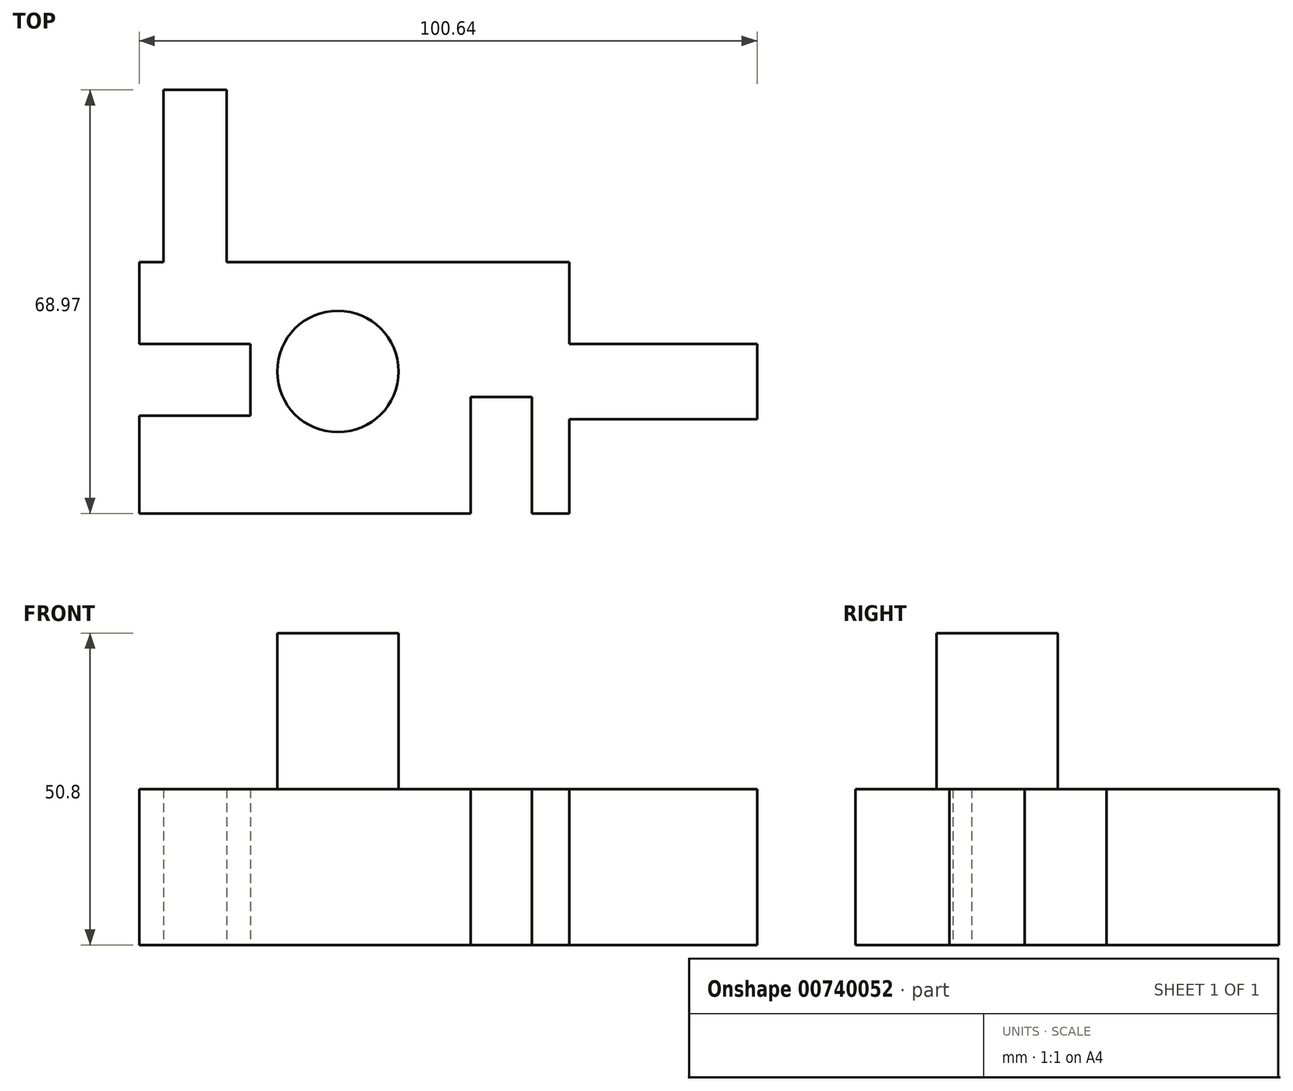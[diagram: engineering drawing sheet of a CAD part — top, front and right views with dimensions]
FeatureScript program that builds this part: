
annotation { "Feature Type Name" : "Feature", "Feature Type Description" : "" }
export const myFeature = defineFeature(function(context is Context, id is Id, definition is map)
    precondition{}
    {
        {
            var Q0;
            Q0=qCreatedBy(makeId("Top.planeOp"),FACE);
            var sketch = newSketch(context, id + "F0", { "sketchPlane" : qUnion([Q0])});
            skLineSegment(sketch, "E0.bottom", {"start": v(0, 0) * mm, "end": v(70.08, 0) * mm});
            skLineSegment(sketch, "E0.top", {"start": v(0, 40.9) * mm, "end": v(70.08, 40.9) * mm});
            skLineSegment(sketch, "E0.left", {"start": v(0, 0) * mm, "end": v(0, 40.9) * mm});
            skLineSegment(sketch, "E0.right", {"start": v(70.08, 0) * mm, "end": v(70.08, 40.9) * mm});
            skLineSegment(sketch, "E1.bottom", {"start": v(70.08, 15.35) * mm, "end": v(100.64, 15.35) * mm});
            skLineSegment(sketch, "E1.top", {"start": v(70.08, 27.57) * mm, "end": v(100.64, 27.57) * mm});
            skLineSegment(sketch, "E1.left", {"start": v(70.08, 15.35) * mm, "end": v(70.08, 27.57) * mm});
            skLineSegment(sketch, "E1.right", {"start": v(100.64, 15.35) * mm, "end": v(100.64, 27.57) * mm});
            skLineSegment(sketch, "E2.bottom", {"start": v(3.96, 40.9) * mm, "end": v(14.24, 40.9) * mm});
            skLineSegment(sketch, "E2.top", {"start": v(3.96, 68.97) * mm, "end": v(14.24, 68.97) * mm});
            skLineSegment(sketch, "E2.left", {"start": v(3.96, 40.9) * mm, "end": v(3.96, 68.97) * mm});
            skLineSegment(sketch, "E2.right", {"start": v(14.24, 40.9) * mm, "end": v(14.24, 68.97) * mm});
            skLineSegment(sketch, "E3.bottom", {"start": v(0, 27.57) * mm, "end": v(18.13, 27.57) * mm});
            skLineSegment(sketch, "E3.top", {"start": v(0, 15.9) * mm, "end": v(18.13, 15.9) * mm});
            skLineSegment(sketch, "E3.left", {"start": v(0, 27.57) * mm, "end": v(0, 15.9) * mm});
            skLineSegment(sketch, "E3.right", {"start": v(18.13, 27.57) * mm, "end": v(18.13, 15.9) * mm});
            skLineSegment(sketch, "E4.bottom", {"start": v(53.97, 0) * mm, "end": v(63.97, 0) * mm});
            skLineSegment(sketch, "E4.top", {"start": v(53.97, 18.96) * mm, "end": v(63.97, 18.96) * mm});
            skLineSegment(sketch, "E4.left", {"start": v(53.97, 0) * mm, "end": v(53.97, 18.96) * mm});
            skLineSegment(sketch, "E4.right", {"start": v(63.97, 0) * mm, "end": v(63.97, 18.96) * mm});
            skSolve(sketch);
        }
        {
            var Q0;
            {var subQ2=sQuery(id+"F0.wireOp",EDGE,"E1.bottom");Q0=makeQuery(id+"F0.imprint","IMPRINT",FACE,{"disambiguationData":[TD([[makeQuery(id+"F0.imprint","IMPRINT",EDGE,{"derivedFrom":subQ2}),1.0]])]});}
            var Q1;
            Q1=makeQuery(id+"F0.imprint","IMPRINT",FACE,{"disambiguationData":[TD([[makeQuery(id+"F0.imprint","IMPRINT",EDGE,{"derivedFrom":sQuery(id+"F0.wireOp",EDGE,"E2.top")}),-1.0]])]});
            var Q2;
            {var subQ7=sQuery(id+"F0.wireOp",EDGE,"E3.bottom");Q2=makeQuery(id+"F0.imprint","IMPRINT",FACE,{"disambiguationData":[TD([[makeQuery(id+"F0.imprint","IMPRINT",EDGE,{"derivedFrom":subQ7}),1.0]])]});}
            extrude(context, id + "F1", {"entities" : qUnion([Q0, Q1, Q2]), "depth" : 25.4 * mm, "offsetDistance" : 25.4 * mm});
        }
        {
            var Q0;
            Q0=makeQuery(id+"F1.opExtrude","CAP_FACE",FACE,{"disambiguationData":[OSD([sQuery(id+"F0.wireOp",EDGE,"E0.bottom"),sQuery(id+"F0.wireOp",EDGE,"E0.top"),sQuery(id+"F0.wireOp",EDGE,"E0.left"),sQuery(id+"F0.wireOp",EDGE,"E0.right"),sQuery(id+"F0.wireOp",EDGE,"E1.bottom"),sQuery(id+"F0.wireOp",EDGE,"E1.top"),sQuery(id+"F0.wireOp",EDGE,"E1.right"),sQuery(id+"F0.wireOp",EDGE,"E2.top"),sQuery(id+"F0.wireOp",EDGE,"E2.left"),sQuery(id+"F0.wireOp",EDGE,"E2.right"),sQuery(id+"F0.wireOp",EDGE,"E3.bottom"),sQuery(id+"F0.wireOp",EDGE,"E3.top"),sQuery(id+"F0.wireOp",EDGE,"E3.right"),sQuery(id+"F0.wireOp",EDGE,"E4.top"),sQuery(id+"F0.wireOp",EDGE,"E4.left"),sQuery(id+"F0.wireOp",EDGE,"E4.right")])],"isStart":false});
            var sketch = newSketch(context, id + "F2", { "sketchPlane" : qUnion([Q0])});
            skCircle(sketch, "E5", {"center": v(32.36, 23.11) * mm, "radius": 9.89 * mm});
            skSolve(sketch);
        }
        {
            var Q0;
            Q0 = qSketchRegion(id + "F2", true);
            extrude(context, id + "F3", {"entities" : qUnion([Q0]), "operationType" : NewBodyOperationType.ADD, "depth" : 25.4 * mm, "offsetDistance" : 25.4 * mm});
        }
    });
